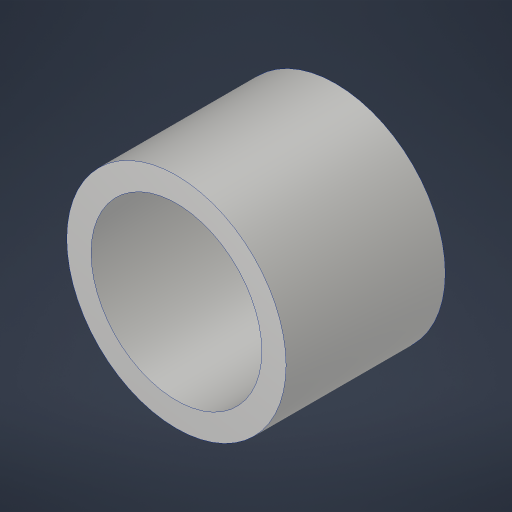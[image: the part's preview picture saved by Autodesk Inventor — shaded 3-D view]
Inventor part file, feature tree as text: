
AUTODESK INVENTOR PART (.ipt)
format: ipt  version: 2023.4 (Build 274418000, 418)  size: 166,912 bytes
history: native  units: in
note: dims shown in document units (in); Inventor stores cm internally (conversion verified against a paired STEP export)
features: extrude x1, sketch x1
ambient origin geometry x8: Origin, YZ Plane, XZ Plane, XY Plane, X Axis, Y Axis, Z Axis, Center Point
bodies: Solid1 (feature_tree)
feature tree (2):
  extrude  "Extrusion1"  Depth=0.82in
  sketch  "Sketch1"  dims[d0=0.125in d1=0.88in d2=0.82in d3=0.0in]
